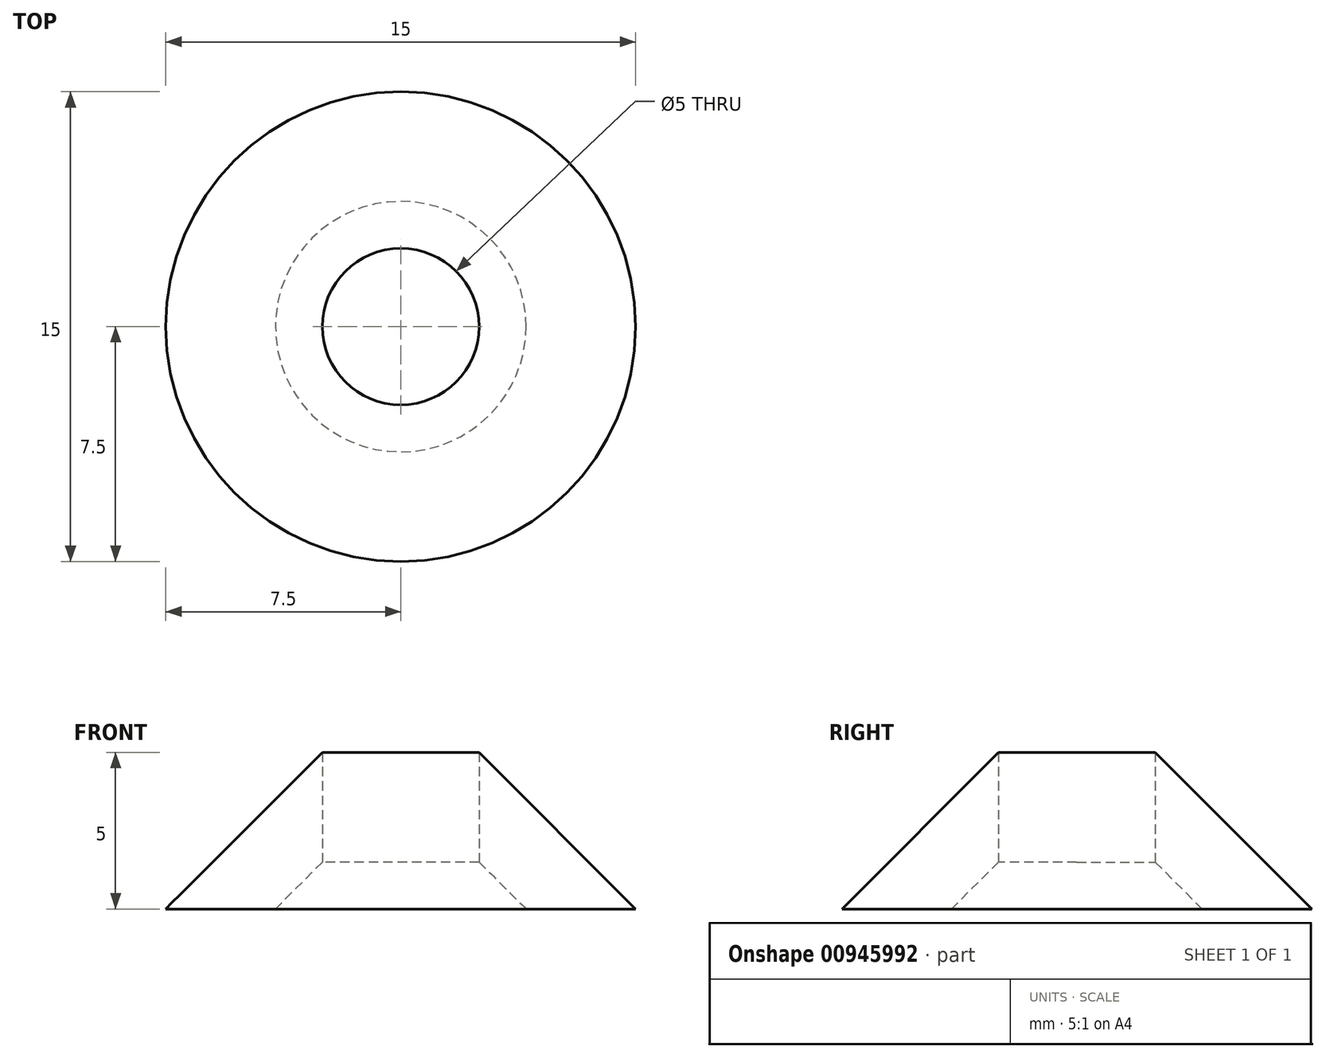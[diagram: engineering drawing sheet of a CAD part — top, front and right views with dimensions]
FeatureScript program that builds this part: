
annotation { "Feature Type Name" : "Feature", "Feature Type Description" : "" }
export const myFeature = defineFeature(function(context is Context, id is Id, definition is map)
    precondition{}
    {
        {
            var Q0;
            Q0=qCreatedBy(makeId("Front.planeOp"),FACE);
            var sketch = newSketch(context, id + "F0", { "sketchPlane" : qUnion([Q0])});
            skLineSegment(sketch, "E0", {"start": v(0, 0) * mm, "end": v(2.5, 0) * mm});
            skLineSegment(sketch, "E1", {"start": v(2.5, 0) * mm, "end": v(2.5, 5) * mm});
            skLineSegment(sketch, "E2", {"start": v(2.5, 5) * mm, "end": v(7.5, 0) * mm});
            skLineSegment(sketch, "E3", {"start": v(7.5, 0) * mm, "end": v(2.5, 0) * mm});
            skLineSegment(sketch, "E4", {"start": v(0, 0) * mm, "end": v(0, 5) * mm});
            skSolve(sketch);
        }
        {
            var Q0;
            Q0=makeQuery(id+"F0.imprint","IMPRINT",FACE,{"disambiguationData":[TD([[makeQuery(id+"F0.imprint","IMPRINT",EDGE,{"derivedFrom":sQuery(id+"F0.wireOp",EDGE,"E1")}),-1.0]])]});
            var Q1;
            Q1=sQuery(id+"F0.wireOp",EDGE,"E4");
            revolve(context, id + "F1", {"surfaceOperationType" : NewSurfaceOperationType.NEW, "entities" : qUnion([Q0]), "axis" : qUnion([Q1]), "revolveType" : RevolveType.FULL});
        }
        {
            var Q0;
            Q0=makeQuery(id+"F1.opRevolve","SWEPT_EDGE",EDGE,{"disambiguationData":[OSD([sQuery(id+"F0.wireOp",EDGE,"E1"),sQuery(id+"F0.wireOp",EDGE,"E3")])]});
            chamfer(context, id + "F2", {"entities" : qUnion([Q0]), "width" : 1.5 * mm, "tangentPropagation" : true});
        }
    });
